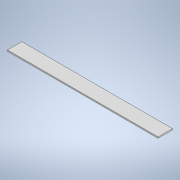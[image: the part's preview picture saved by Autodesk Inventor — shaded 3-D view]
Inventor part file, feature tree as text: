
AUTODESK INVENTOR PART (.ipt)
format: ipt  version: 2022 (Build 260153000, 153)  size: 93,184 bytes
history: native  units: mm
features: extrude x1, sketch x1
ambient origin geometry x8: Origin, YZ Plane, XZ Plane, XY Plane, X Axis, Y Axis, Z Axis, Center Point
bodies: Solid1 (feature_tree)
feature tree (2):
  extrude  "Extrusion1"  Depth=100.0mm
  sketch  "Sketch1"  dims[d0=1050.0mm d1=100.0mm d2=9.0mm d3=0.0mm]
